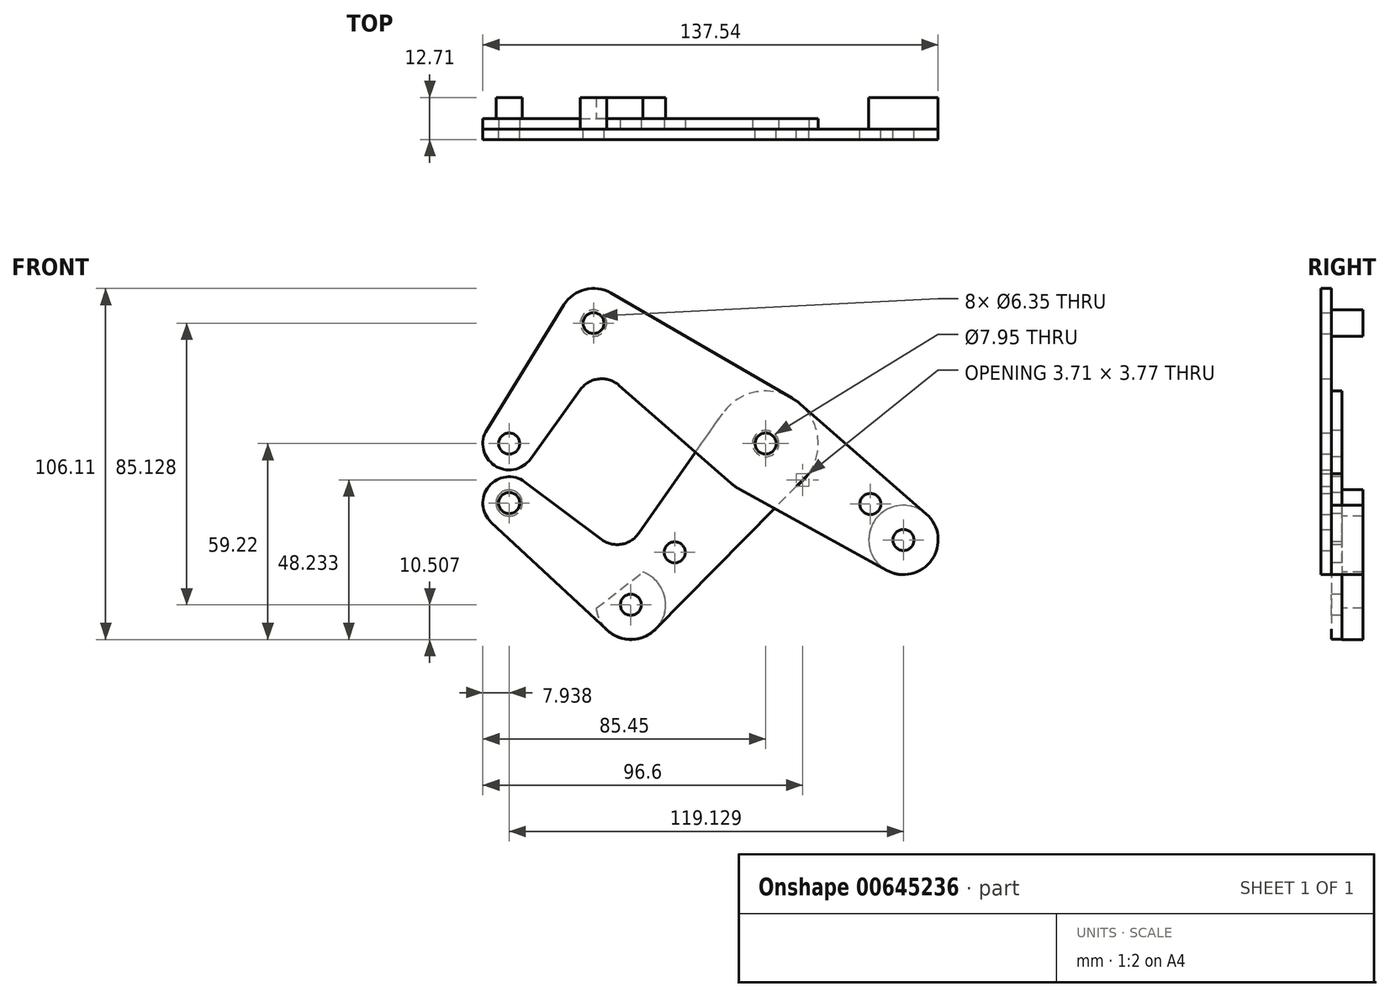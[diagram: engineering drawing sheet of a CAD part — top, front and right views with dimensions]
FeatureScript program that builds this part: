
annotation { "Feature Type Name" : "Feature", "Feature Type Description" : "" }
export const myFeature = defineFeature(function(context is Context, id is Id, definition is map)
    precondition{}
    {
        {
            var Q0;
            Q0=qCreatedBy(makeId("Front.planeOp"),FACE);
            var sketch = newSketch(context, id + "F0", { "sketchPlane" : qUnion([Q0])});
            skLineSegment(sketch, "E0", {"start": v(-77.51, 0) * mm, "end": v(-52.02, 36.41) * mm, "construction": true});
            skLineSegment(sketch, "E1", {"start": v(-52.02, 36.41) * mm, "end": v(41.62, -29.13) * mm, "construction": true});
            skCircle(sketch, "E2", {"center": v(-77.51, 0) * mm, "radius": 3.18 * mm});
            skCircle(sketch, "E3", {"center": v(-77.51, 0) * mm, "radius": 7.94 * mm});
            skCircle(sketch, "E4", {"center": v(-52.02, 36.41) * mm, "radius": 3.18 * mm});
            skCircle(sketch, "E5", {"center": v(-52.02, 36.41) * mm, "radius": 10.48 * mm});
            skCircle(sketch, "E6", {"center": v(0, 0) * mm, "radius": 15.88 * mm});
            skCircle(sketch, "E7", {"center": v(0, 0) * mm, "radius": 3.18 * mm});
            skCircle(sketch, "E8", {"center": v(0, 0) * mm, "radius": 3.98 * mm});
            skCircle(sketch, "E9", {"center": v(41.62, -29.13) * mm, "radius": 10.48 * mm});
            skCircle(sketch, "E10", {"center": v(41.62, -29.13) * mm, "radius": 3.18 * mm});
            skCircle(sketch, "E11", {"center": v(31.63, -18.27) * mm, "radius": 3.18 * mm});
            skLineSegment(sketch, "E12", {"start": v(-84.26, 4.17) * mm, "end": v(-60.93, 41.92) * mm});
            skLineSegment(sketch, "E13", {"start": v(-71.07, -4.64) * mm, "end": v(-56, 16.28) * mm});
            skArc(sketch, "E14.filletArc", {"start": v(-44.33, 17.63) * mm, "mid": v(-50.46, 19.54) * mm, "end": v(-56, 16.28) * mm});
            skLineSegment(sketch, "E15", {"start": v(0, 0) * mm, "end": v(-40.73, -48.71) * mm, "construction": true});
            skCircle(sketch, "E16", {"center": v(-40.73, -48.71) * mm, "radius": 10.48 * mm});
            skCircle(sketch, "E17", {"center": v(-40.73, -48.71) * mm, "radius": 3.18 * mm});
            skCircle(sketch, "E18", {"center": v(-27.49, -32.87) * mm, "radius": 3.18 * mm});
            skLineSegment(sketch, "E19", {"start": v(-46.76, 45.48) * mm, "end": v(7.97, 13.73) * mm});
            skLineSegment(sketch, "E20", {"start": v(10.43, 11.96) * mm, "end": v(48.5, -21.24) * mm});
            skLineSegment(sketch, "E21", {"start": v(36.55, -38.3) * mm, "end": v(-7.67, -13.9) * mm});
            skLineSegment(sketch, "E22", {"start": v(-44.33, 17.63) * mm, "end": v(-10.44, -11.96) * mm});
            skLineSegment(sketch, "E23", {"start": v(-40.73, -48.71) * mm, "end": v(-77.51, -17.96) * mm, "construction": true});
            skCircle(sketch, "E24", {"center": v(-77.51, -17.96) * mm, "radius": 7.94 * mm});
            skCircle(sketch, "E25", {"center": v(-77.51, -17.96) * mm, "radius": 3.18 * mm});
            skLineSegment(sketch, "E26", {"start": v(-72.75, -11.6) * mm, "end": v(-49.65, -28.93) * mm});
            skLineSegment(sketch, "E27", {"start": v(-82.92, -23.77) * mm, "end": v(-47.87, -56.38) * mm});
            skLineSegment(sketch, "E28", {"start": v(-38.37, -27.13) * mm, "end": v(-13, 9.1) * mm});
            skLineSegment(sketch, "E29", {"start": v(13, -9.1) * mm, "end": v(-33.27, -56.07) * mm});
            skArc(sketch, "E30.filletArc", {"start": v(-49.65, -28.93) * mm, "mid": v(-43.63, -30.42) * mm, "end": v(-38.37, -27.13) * mm});
            skSolve(sketch);
        }
        {
            var Q0;
            Q0=makeQuery(id+"F0.imprint","IMPRINT",FACE,{"disambiguationData":[TD([[makeQuery(id+"F0.imprint","IMPRINT",EDGE,{"derivedFrom":sQuery(id+"F0.wireOp",EDGE,"E4")}),-1.0]])]});
            var Q1;
            {var subQ0=sQuery(id+"F0.wireOp",EDGE,"E12");Q1=makeQuery(id+"F0.imprint","IMPRINT",FACE,{"disambiguationData":[TD([[makeQuery(id+"F0.imprint","IMPRINT",EDGE,{"derivedFrom":subQ0}),-1.0]])]});}
            var Q2;
            Q2=makeQuery(id+"F0.imprint","IMPRINT",FACE,{"disambiguationData":[TD([[makeQuery(id+"F0.imprint","IMPRINT",EDGE,{"derivedFrom":sQuery(id+"F0.wireOp",EDGE,"E7")}),-1.0]])]});
            var Q3;
            Q3=makeQuery(id+"F0.imprint","IMPRINT",FACE,{"disambiguationData":[TD([[makeQuery(id+"F0.imprint","IMPRINT",EDGE,{"derivedFrom":sQuery(id+"F0.wireOp",EDGE,"E11")}),-1.0]])]});
            var Q4;
            Q4=makeQuery(id+"F0.imprint","IMPRINT",FACE,{"disambiguationData":[TD([[makeQuery(id+"F0.imprint","IMPRINT",EDGE,{"derivedFrom":sQuery(id+"F0.wireOp",EDGE,"E10")}),-1.0]])]});
            var Q5;
            Q5=makeQuery(id+"F0.imprint","IMPRINT",FACE,{"disambiguationData":[TD([[makeQuery(id+"F0.imprint","IMPRINT",EDGE,{"derivedFrom":sQuery(id+"F0.wireOp",EDGE,"E2")}),-1.0]])]});
            var Q6;
            {var subQ0=sQuery(id+"F0.wireOp",EDGE,"E22");var subQ1=sQuery(id+"F0.wireOp",EDGE,"E6");var subQ2=makeQuery(id+"F0.imprint","INTERSECT",VERTEX,{"derivedFrom":[subQ1,subQ0]});Q6=makeQuery(id+"F0.imprint","IMPRINT",FACE,{"disambiguationData":[TD([[makeQuery(id+"F0.imprint","IMPRINT",EDGE,{"disambiguationData":[TD([[subQ2,1.0]])],"derivedFrom":subQ1}),-1.0]])]});}
            var Q7;
            {var subQ0=sQuery(id+"F0.wireOp",EDGE,"E21");var subQ1=sQuery(id+"F0.wireOp",EDGE,"E6");var subQ2=makeQuery(id+"F0.imprint","INTERSECT",VERTEX,{"derivedFrom":[subQ1,subQ0]});Q7=makeQuery(id+"F0.imprint","IMPRINT",FACE,{"disambiguationData":[TD([[makeQuery(id+"F0.imprint","IMPRINT",EDGE,{"disambiguationData":[TD([[subQ2,-1.0]])],"derivedFrom":subQ1}),-1.0]])]});}
            var Q8;
            Q8=makeQuery(id+"F0.imprint","IMPRINT",FACE,{"disambiguationData":[TD([[makeQuery(id+"F0.imprint","IMPRINT",EDGE,{"derivedFrom":sQuery(id+"F0.wireOp",EDGE,"E8")}),-1.0]])]});
            extrude(context, id + "F1", {"entities" : qUnion([Q0, Q1, Q2, Q3, Q4, Q5, Q6, Q7, Q8]), "depth" : 3.17 * mm, "offsetDistance" : 25.4 * mm});
        }
        {
            var Q0;
            Q0=makeQuery(id+"F0.imprint","IMPRINT",FACE,{"disambiguationData":[TD([[makeQuery(id+"F0.imprint","IMPRINT",EDGE,{"derivedFrom":sQuery(id+"F0.wireOp",EDGE,"E8")}),-1.0]])]});
            var Q1;
            {var subQ0=sQuery(id+"F0.wireOp",EDGE,"E22");var subQ1=sQuery(id+"F0.wireOp",EDGE,"E6");var subQ2=makeQuery(id+"F0.imprint","INTERSECT",VERTEX,{"derivedFrom":[subQ1,subQ0]});Q1=makeQuery(id+"F0.imprint","IMPRINT",FACE,{"disambiguationData":[TD([[makeQuery(id+"F0.imprint","IMPRINT",EDGE,{"disambiguationData":[TD([[subQ2,1.0]])],"derivedFrom":subQ1}),-1.0]])]});}
            var Q2;
            {var subQ0=sQuery(id+"F0.wireOp",EDGE,"E21");var subQ1=sQuery(id+"F0.wireOp",EDGE,"E6");var subQ2=makeQuery(id+"F0.imprint","INTERSECT",VERTEX,{"derivedFrom":[subQ1,subQ0]});Q2=makeQuery(id+"F0.imprint","IMPRINT",FACE,{"disambiguationData":[TD([[makeQuery(id+"F0.imprint","IMPRINT",EDGE,{"disambiguationData":[TD([[subQ2,-1.0]])],"derivedFrom":subQ1}),-1.0]])]});}
            var Q3;
            Q3=makeQuery(id+"F0.imprint","IMPRINT",FACE,{"disambiguationData":[TD([[makeQuery(id+"F0.imprint","IMPRINT",EDGE,{"derivedFrom":sQuery(id+"F0.wireOp",EDGE,"E18")}),-1.0]])]});
            var Q4;
            Q4=makeQuery(id+"F0.imprint","IMPRINT",FACE,{"disambiguationData":[TD([[makeQuery(id+"F0.imprint","IMPRINT",EDGE,{"derivedFrom":sQuery(id+"F0.wireOp",EDGE,"E17")}),-1.0]])]});
            var Q5;
            Q5=makeQuery(id+"F0.imprint","IMPRINT",FACE,{"disambiguationData":[TD([[makeQuery(id+"F0.imprint","IMPRINT",EDGE,{"derivedFrom":sQuery(id+"F0.wireOp",EDGE,"E25")}),-1.0]])]});
            extrude(context, id + "F2", {"entities" : qUnion([Q0, Q1, Q2, Q3, Q4, Q5]), "oppositeDirection" : true, "depth" : 3.17 * mm, "offsetDistance" : 25.4 * mm});
        }
        {
            var Q0;
            Q0=makeQuery(id+"F1.opExtrude","CAP_FACE",FACE,{"disambiguationData":[OSD([sQuery(id+"F0.wireOp",EDGE,"E4"),sQuery(id+"F0.wireOp",EDGE,"E5"),sQuery(id+"F0.wireOp",EDGE,"E6"),sQuery(id+"F0.wireOp",EDGE,"E7"),sQuery(id+"F0.wireOp",EDGE,"E9"),sQuery(id+"F0.wireOp",EDGE,"E10"),sQuery(id+"F0.wireOp",EDGE,"E11"),sQuery(id+"F0.wireOp",EDGE,"E12"),sQuery(id+"F0.wireOp",EDGE,"E13"),sQuery(id+"F0.wireOp",EDGE,"E14.filletArc"),sQuery(id+"F0.wireOp",EDGE,"E3"),sQuery(id+"F0.wireOp",EDGE,"E2"),sQuery(id+"F0.wireOp",EDGE,"E19"),sQuery(id+"F0.wireOp",EDGE,"E20"),sQuery(id+"F0.wireOp",EDGE,"E21"),sQuery(id+"F0.wireOp",EDGE,"E22"),sQuery(id+"F0.wireOp",EDGE,"E29")])],"isStart":false});
            var sketch = newSketch(context, id + "F3", { "sketchPlane" : qUnion([Q0])});
            skCircle(sketch, "E31", {"center": v(-52.02, 36.41) * mm, "radius": 3.98 * mm});
            skCircle(sketch, "E32.0", {"center": v(41.62, -29.13) * mm, "radius": 10.48 * mm});
            skSolve(sketch);
        }
        {
            var Q0;
            Q0=makeQuery(id+"F2.opExtrude","CAP_FACE",FACE,{"disambiguationData":[OSD([sQuery(id+"F0.wireOp",EDGE,"E6"),sQuery(id+"F0.wireOp",EDGE,"E8"),sQuery(id+"F0.wireOp",EDGE,"E16"),sQuery(id+"F0.wireOp",EDGE,"E17"),sQuery(id+"F0.wireOp",EDGE,"E18"),sQuery(id+"F0.wireOp",EDGE,"E24"),sQuery(id+"F0.wireOp",EDGE,"E25"),sQuery(id+"F0.wireOp",EDGE,"E26"),sQuery(id+"F0.wireOp",EDGE,"E27"),sQuery(id+"F0.wireOp",EDGE,"E28"),sQuery(id+"F0.wireOp",EDGE,"E29"),sQuery(id+"F0.wireOp",EDGE,"E30.filletArc")])],"isStart":false});
            var sketch = newSketch(context, id + "F4", { "sketchPlane" : qUnion([Q0])});
            skCircle(sketch, "E33", {"center": v(77.51, -17.96) * mm, "radius": 3.98 * mm});
            skLineSegment(sketch, "E34", {"start": v(78.42, 0) * mm, "end": v(40.73, -48.71) * mm, "construction": true});
            skArc(sketch, "E35", {"start": v(37.08, -38.86) * mm, "mid": v(34.3, -57.03) * mm, "end": v(51.2, -49.77) * mm});
            skLineSegment(sketch, "E36", {"start": v(37.08, -38.86) * mm, "end": v(51.2, -49.77) * mm});
            skSolve(sketch);
        }
        {
            var Q0;
            Q0=qCreatedBy(makeId("Front.planeOp"),FACE);
            cPlane(context, id + "F5", {"entities" : qUnion([Q0]), "cplaneType" : CPlaneType.OFFSET, "offset" : 9.52 * mm, "oppositeDirection" : true, "width" : 152.4 * mm, "height" : 152.4 * mm});
        }
        {
            var Q0;
            Q0 = qSketchRegion(id + "F3", true);
            var Q1;
            Q1 = qSketchRegion(id + "F4", true);
            var Q2;
            Q2=qCreatedBy(id+"F5.planeOp",FACE);
            extrude(context, id + "F6", {"entities" : qUnion([Q0, Q1]), "endBound" : BoundingType.UP_TO_SURFACE, "oppositeDirection" : true, "depth" : 25.4 * mm, "endBoundEntityFace" : qUnion([Q2]), "offsetDistance" : 25.4 * mm});
        }
        {
            var Q0;
            Q0=makeQuery(id+"F1.opExtrude","SWEPT_BODY",BODY,{"disambiguationData":[OSD([sQuery(id+"F0.wireOp",EDGE,"E4"),sQuery(id+"F0.wireOp",EDGE,"E5"),sQuery(id+"F0.wireOp",EDGE,"E6"),sQuery(id+"F0.wireOp",EDGE,"E7"),sQuery(id+"F0.wireOp",EDGE,"E9"),sQuery(id+"F0.wireOp",EDGE,"E10"),sQuery(id+"F0.wireOp",EDGE,"E11"),sQuery(id+"F0.wireOp",EDGE,"E12"),sQuery(id+"F0.wireOp",EDGE,"E13"),sQuery(id+"F0.wireOp",EDGE,"E14.filletArc"),sQuery(id+"F0.wireOp",EDGE,"E3"),sQuery(id+"F0.wireOp",EDGE,"E2"),sQuery(id+"F0.wireOp",EDGE,"E19"),sQuery(id+"F0.wireOp",EDGE,"E20"),sQuery(id+"F0.wireOp",EDGE,"E21"),sQuery(id+"F0.wireOp",EDGE,"E22"),sQuery(id+"F0.wireOp",EDGE,"E29")])]});
            var Q1;
            Q1=makeQuery(id+"F2.opExtrude","SWEPT_BODY",BODY,{"disambiguationData":[OSD([sQuery(id+"F0.wireOp",EDGE,"E6"),sQuery(id+"F0.wireOp",EDGE,"E8"),sQuery(id+"F0.wireOp",EDGE,"E16"),sQuery(id+"F0.wireOp",EDGE,"E17"),sQuery(id+"F0.wireOp",EDGE,"E18"),sQuery(id+"F0.wireOp",EDGE,"E24"),sQuery(id+"F0.wireOp",EDGE,"E25"),sQuery(id+"F0.wireOp",EDGE,"E26"),sQuery(id+"F0.wireOp",EDGE,"E27"),sQuery(id+"F0.wireOp",EDGE,"E28"),sQuery(id+"F0.wireOp",EDGE,"E29"),sQuery(id+"F0.wireOp",EDGE,"E30.filletArc")])]});
            var Q2;
            Q2=makeQuery(id+"F6.opExtrude","SWEPT_BODY",BODY,{"disambiguationData":[OSD([sQuery(id+"F3.wireOp",EDGE,"E32.0")])]});
            var Q3;
            Q3=makeQuery(id+"F6.opExtrude","SWEPT_BODY",BODY,{"disambiguationData":[OSD([sQuery(id+"F4.wireOp",EDGE,"E33")])]});
            var Q4;
            Q4=makeQuery(id+"F6.opExtrude","SWEPT_BODY",BODY,{"disambiguationData":[OSD([sQuery(id+"F3.wireOp",EDGE,"E31")])]});
            var Q5;
            Q5=makeQuery(id+"F6.opExtrude","SWEPT_BODY",BODY,{"disambiguationData":[OSD([sQuery(id+"F4.wireOp",EDGE,"E35"),sQuery(id+"F4.wireOp",EDGE,"E36")])]});
            booleanBodies(context, id + "F7", {"operationType" : BooleanOperationType.SUBTRACTION, "tools" : qUnion([Q0, Q1]), "targets" : qUnion([Q2, Q3, Q4, Q5]), "keepTools" : true});
        }
    });
